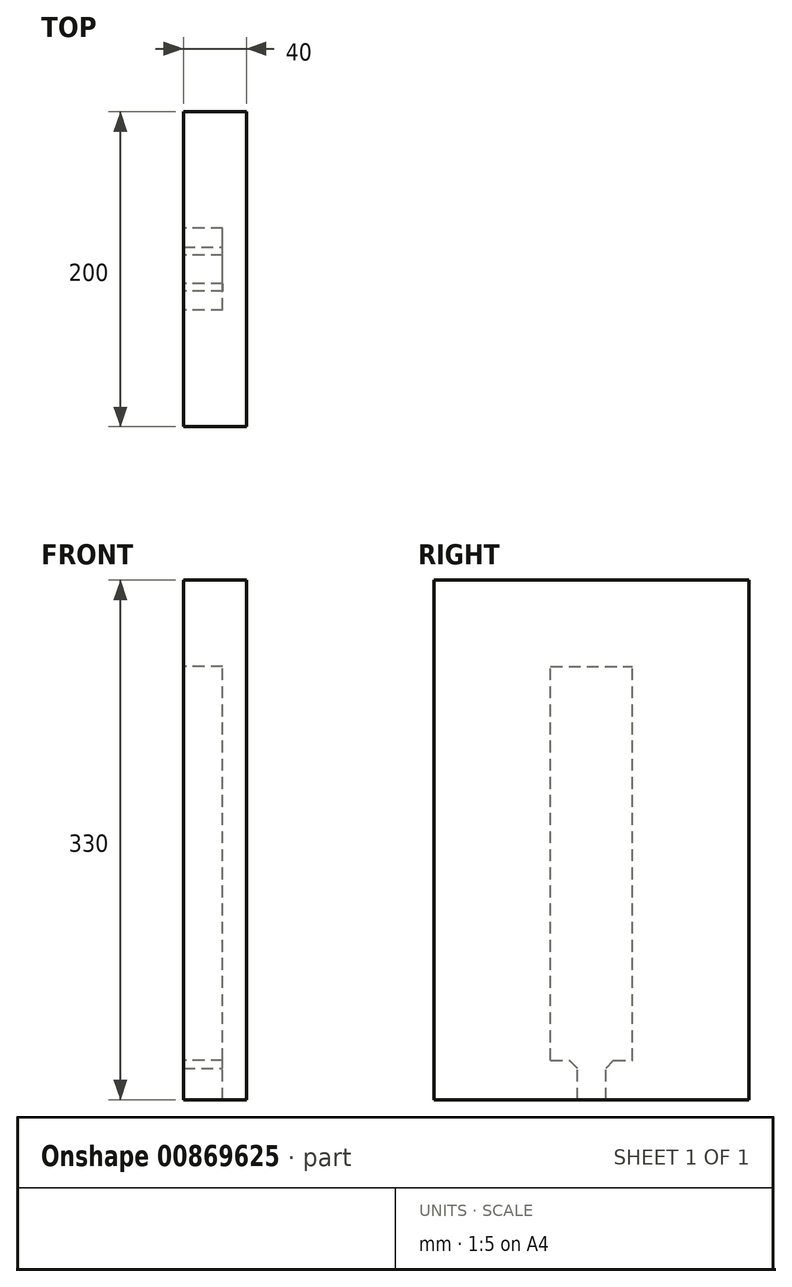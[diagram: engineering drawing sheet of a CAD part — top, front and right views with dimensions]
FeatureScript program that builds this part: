
annotation { "Feature Type Name" : "Feature", "Feature Type Description" : "" }
export const myFeature = defineFeature(function(context is Context, id is Id, definition is map)
    precondition{}
    {
        {
            var Q0;
            Q0=qCreatedBy(makeId("Top.planeOp"),FACE);
            var sketch = newSketch(context, id + "F0", { "sketchPlane" : qUnion([Q0])});
            skLineSegment(sketch, "E0.bottom", {"start": v(20, -100) * mm, "end": v(-20, -100) * mm});
            skLineSegment(sketch, "E0.top", {"start": v(20, 100) * mm, "end": v(-20, 100) * mm});
            skLineSegment(sketch, "E0.left", {"start": v(20, -100) * mm, "end": v(20, 100) * mm});
            skLineSegment(sketch, "E0.right", {"start": v(-20, -100) * mm, "end": v(-20, 100) * mm});
            skPoint(sketch, "E0.middle", {"position": v(0, 0) * mm});
            skSolve(sketch);
        }
        {
            var Q0;
            Q0 = qSketchRegion(id + "F0", true);
            extrude(context, id + "F1", {"entities" : qUnion([Q0]), "depth" : 330 * mm, "offsetDistance" : 25 * mm});
        }
        {
            var Q0;
            Q0=makeQuery(id+"F1.opExtrude","SWEPT_FACE",FACE,{"disambiguationData":[OSD([sQuery(id+"F0.wireOp",EDGE,"E0.right")])]});
            var sketch = newSketch(context, id + "F2", { "sketchPlane" : qUnion([Q0])});
            skLineSegment(sketch, "E1.bottom", {"start": v(26, 25) * mm, "end": v(-26, 25) * mm});
            skLineSegment(sketch, "E1.top", {"start": v(26, 275) * mm, "end": v(-26, 275) * mm});
            skLineSegment(sketch, "E1.left", {"start": v(26, 25) * mm, "end": v(26, 275) * mm});
            skLineSegment(sketch, "E1.right", {"start": v(-26, 25) * mm, "end": v(-26, 275) * mm});
            skPoint(sketch, "E1.middle", {"position": v(0, 150) * mm});
            skPoint(sketch, "E1.middle.positionSnap0", {"position": v(0, 0) * mm});
            skPoint(sketch, "E1.centerSnap0", {"position": v(0, 0) * mm});
            skLineSegment(sketch, "E2", {"start": v(0, 25) * mm, "end": v(0, 0) * mm});
            skLineSegment(sketch, "E3.bottom", {"start": v(9, 0) * mm, "end": v(-9, 0) * mm});
            skLineSegment(sketch, "E3.top", {"start": v(9, 25) * mm, "end": v(-9, 25) * mm});
            skLineSegment(sketch, "E3.left", {"start": v(9, 0) * mm, "end": v(9, 25) * mm});
            skLineSegment(sketch, "E3.right", {"start": v(-9, 0) * mm, "end": v(-9, 25) * mm});
            skPoint(sketch, "E3.middle", {"position": v(0, 12.5) * mm});
            skSolve(sketch);
        }
        {
            var Q0;
            Q0 = qSketchRegion(id + "F2", true);
            extrude(context, id + "F3", {"entities" : qUnion([Q0]), "operationType" : NewBodyOperationType.REMOVE, "oppositeDirection" : true, "depth" : 25 * mm, "offsetDistance" : 25 * mm});
        }
        {
            var Q0;
            Q0=makeQuery(id+"F3.boolean.opBoolean","COPY",EDGE,{"derivedFrom":makeQuery(id+"F3.opExtrude","SWEPT_EDGE",EDGE,{"disambiguationData":[OSD([sQuery(id+"F2.wireOp",EDGE,"E1.bottom"),sQuery(id+"F2.wireOp",EDGE,"E3.top"),sQuery(id+"F2.wireOp",EDGE,"E3.right")])]})});
            var Q1;
            Q1=makeQuery(id+"F3.boolean.opBoolean","COPY",EDGE,{"derivedFrom":makeQuery(id+"F3.opExtrude","SWEPT_EDGE",EDGE,{"disambiguationData":[OSD([sQuery(id+"F2.wireOp",EDGE,"E1.bottom"),sQuery(id+"F2.wireOp",EDGE,"E3.top"),sQuery(id+"F2.wireOp",EDGE,"E3.left")])]})});
            chamfer(context, id + "F4", {"entities" : qUnion([Q0, Q1]), "width" : 5 * mm, "tangentPropagation" : true});
        }
    });
